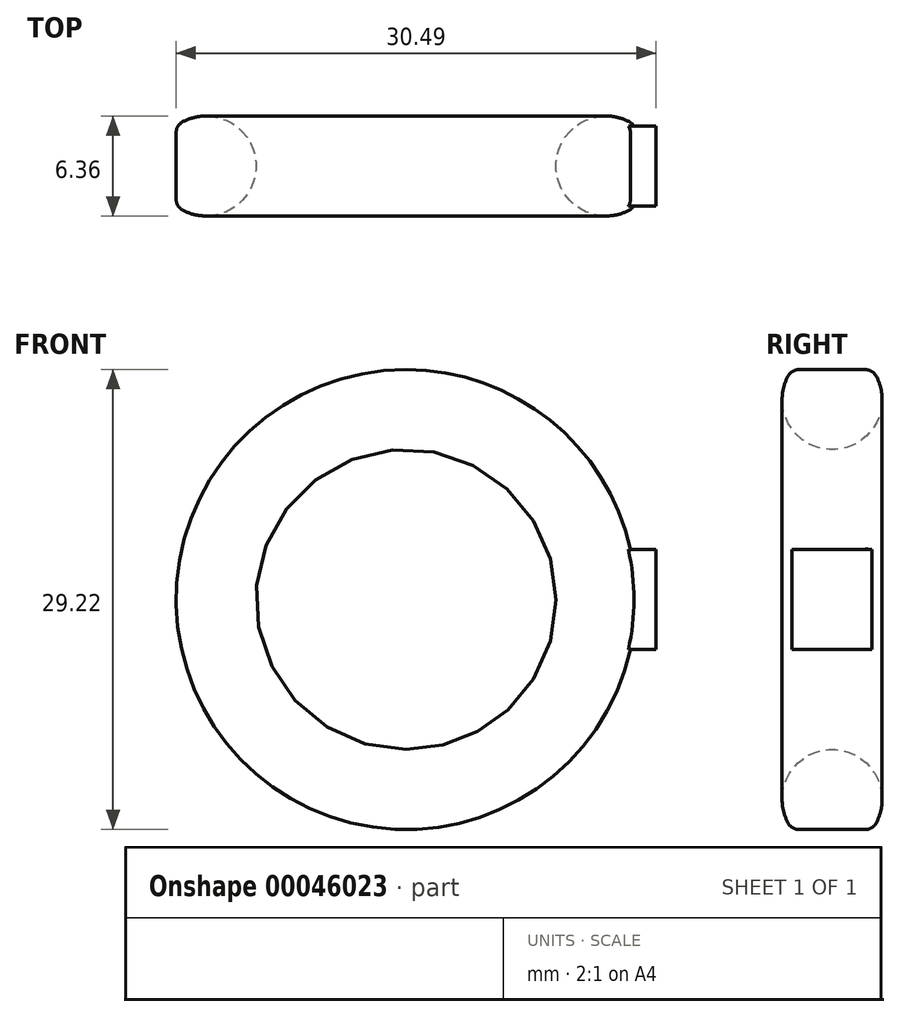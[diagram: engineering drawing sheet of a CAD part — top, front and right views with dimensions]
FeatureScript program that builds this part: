
annotation { "Feature Type Name" : "Feature", "Feature Type Description" : "" }
export const myFeature = defineFeature(function(context is Context, id is Id, definition is map)
    precondition{}
    {
        {
            var Q0;
            Q0=qCreatedBy(makeId("Top.planeOp"),FACE);
            var sketch = newSketch(context, id + "F0", { "sketchPlane" : qUnion([Q0])});
            skLineSegment(sketch, "E0", {"start": v(0, 0) * mm, "end": v(0, 14.5) * mm, "construction": true});
            skArc(sketch, "E1", {"start": v(14.6, 2.54) * mm, "mid": v(9.53, 0) * mm, "end": v(14.6, -2.54) * mm});
            skLineSegment(sketch, "E2", {"start": v(14.6, 2.54) * mm, "end": v(14.6, -2.54) * mm});
            skSolve(sketch);
        }
        {
            var Q0;
            Q0=makeQuery(id+"F0.imprint","IMPRINT",FACE,{"disambiguationData":[TD([[makeQuery(id+"F0.imprint","IMPRINT",EDGE,{"derivedFrom":sQuery(id+"F0.wireOp",EDGE,"E1")}),1.0]])]});
            var Q1;
            Q1=sQuery(id+"F0.wireOp",EDGE,"E0");
            revolve(context, id + "F1", {"entities" : qUnion([Q0]), "axis" : qUnion([Q1]), "revolveType" : RevolveType.FULL});
        }
        {
            var Q0;
            {var subQ0=sQuery(id+"F0.wireOp",EDGE,"E1");var subQ1=sQuery(id+"F0.wireOp",EDGE,"E2");Q0=makeQuery(id+"F1.opRevolve","SWEPT_EDGE",EDGE,{"disambiguationData":[OSD([subQ0,subQ1]),TDD([makeQuery(id+"F0.imprint","INTERSECT",VERTEX,{"disambiguationData":[OD(0.0)],"derivedFrom":[subQ0,subQ1]})])]});}
            var Q1;
            {var subQ0=sQuery(id+"F0.wireOp",EDGE,"E1");var subQ1=sQuery(id+"F0.wireOp",EDGE,"E2");Q1=makeQuery(id+"F1.opRevolve","SWEPT_EDGE",EDGE,{"disambiguationData":[OSD([subQ0,subQ1]),TDD([makeQuery(id+"F0.imprint","INTERSECT",VERTEX,{"disambiguationData":[OD(1.0)],"derivedFrom":[subQ0,subQ1]})])]});}
            fillet(context, id + "F2", {"entities" : qUnion([Q0, Q1]), "radius" : 0.8 * mm, "tangentPropagation" : true, "allowEdgeOverflow" : false});
        }
        {
            var Q0;
            Q0=qCreatedBy(makeId("Top.planeOp"),FACE);
            var sketch = newSketch(context, id + "F3", { "sketchPlane" : qUnion([Q0])});
            skLineSegment(sketch, "E3.bottom", {"start": v(13.97, 2.54) * mm, "end": v(15.88, 2.54) * mm});
            skLineSegment(sketch, "E3.top", {"start": v(13.97, -2.54) * mm, "end": v(15.88, -2.54) * mm});
            skLineSegment(sketch, "E3.left", {"start": v(13.97, 2.54) * mm, "end": v(13.97, -2.54) * mm});
            skLineSegment(sketch, "E3.right", {"start": v(15.88, 2.54) * mm, "end": v(15.88, -2.54) * mm});
            skSolve(sketch);
        }
        {
            var Q0;
            Q0=makeQuery(id+"F3.imprint","IMPRINT",FACE,{"disambiguationData":[TD([[makeQuery(id+"F3.imprint","IMPRINT",EDGE,{"derivedFrom":sQuery(id+"F3.wireOp",EDGE,"E3.bottom")}),-1.0]])]});
            extrude(context, id + "F4", {"entities" : qUnion([Q0]), "operationType" : NewBodyOperationType.ADD, "endBound" : BoundingType.SYMMETRIC, "depth" : 6.35 * mm});
        }
    });
